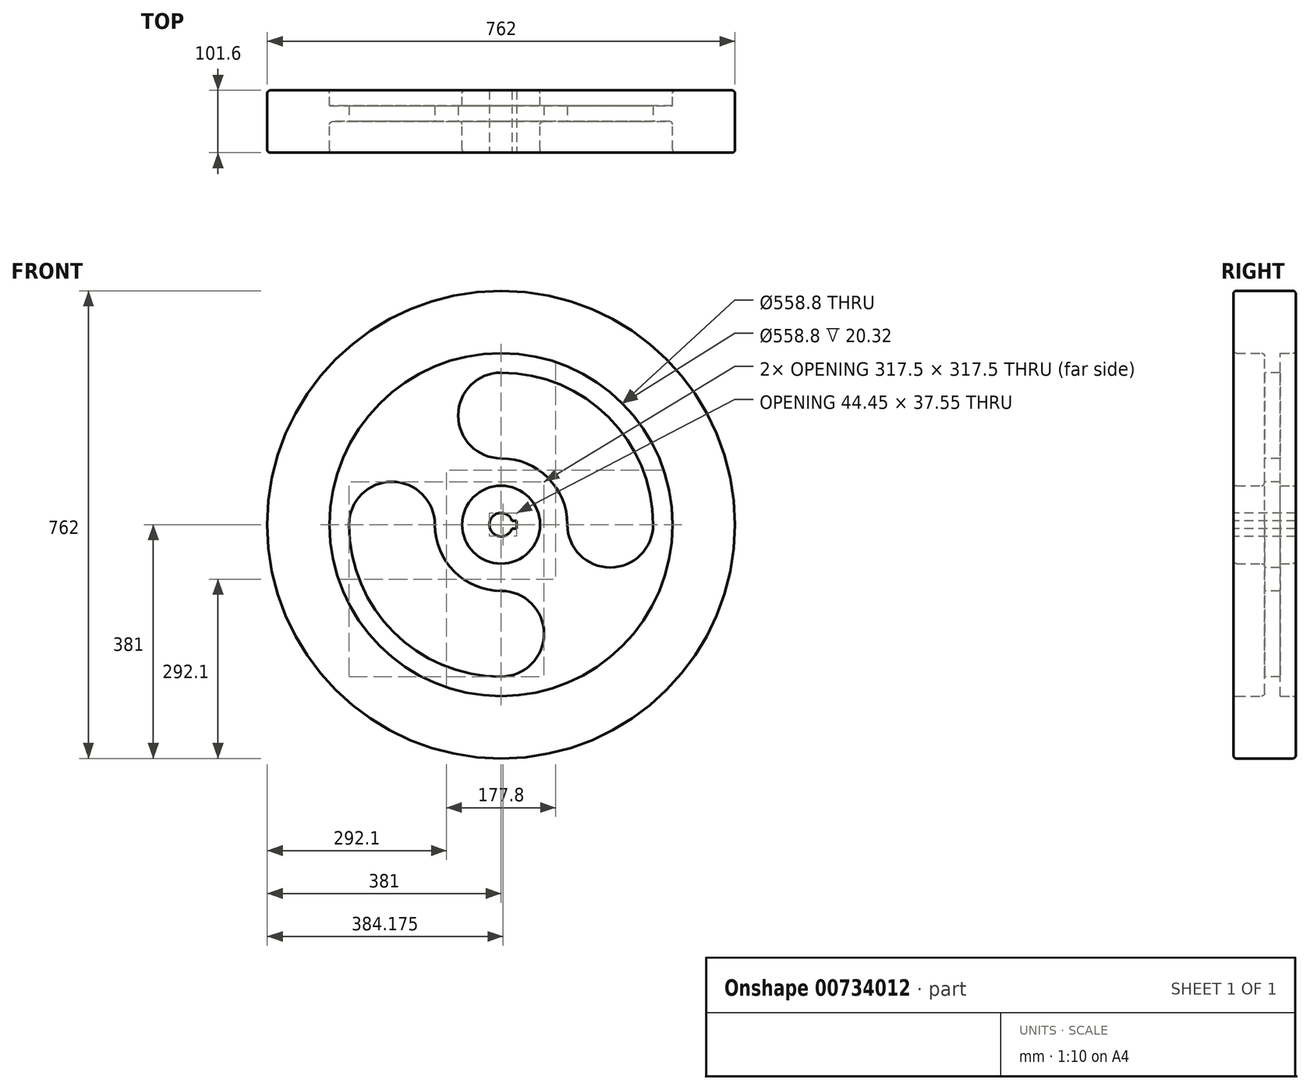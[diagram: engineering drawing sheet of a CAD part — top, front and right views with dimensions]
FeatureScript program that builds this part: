
annotation { "Feature Type Name" : "Feature", "Feature Type Description" : "" }
export const myFeature = defineFeature(function(context is Context, id is Id, definition is map)
    precondition{}
    {
        {
            var Q0;
            Q0=qCreatedBy(makeId("Front.planeOp"),FACE);
            var sketch = newSketch(context, id + "F0", { "sketchPlane" : qUnion([Q0])});
            skCircle(sketch, "E0", {"center": v(0, 0) * mm, "radius": 381 * mm});
            skSolve(sketch);
        }
        {
            var Q0;
            Q0 = qSketchRegion(id + "F0", true);
            extrude(context, id + "F1", {"entities" : qUnion([Q0]), "depth" : 25.4 * mm, "offsetDistance" : 25.4 * mm, "symmetric" : true});
        }
        {
            var Q0;
            Q0=makeQuery(id+"F1.opExtrude","CAP_FACE",FACE,{"disambiguationData":[OSD([sQuery(id+"F0.wireOp",EDGE,"E0")])],"isStart":false});
            var sketch = newSketch(context, id + "F2", { "sketchPlane" : qUnion([Q0])});
            skCircle(sketch, "E1", {"center": v(0, 0) * mm, "radius": 279.4 * mm});
            skCircle(sketch, "E2", {"center": v(0, 0) * mm, "radius": 63.5 * mm});
            skSolve(sketch);
        }
        {
            var Q0;
            Q0=makeQuery(id+"F2.imprint","IMPRINT",FACE,{"disambiguationData":[TD([[makeQuery(id+"F2.imprint","IMPRINT",EDGE,{"derivedFrom":sQuery(id+"F2.wireOp",EDGE,"E1")}),-1.0]])]});
            var Q1;
            Q1=makeQuery(id+"F2.imprint","IMPRINT",FACE,{"disambiguationData":[TD([[makeQuery(id+"F2.imprint","IMPRINT",EDGE,{"derivedFrom":sQuery(id+"F2.wireOp",EDGE,"E2")}),1.0]])]});
            extrude(context, id + "F3", {"entities" : qUnion([Q0, Q1]), "operationType" : NewBodyOperationType.ADD, "depth" : 101.6 * mm, "offsetDistance" : 25.4 * mm, "symmetric" : true});
        }
        {
            var Q0;
            Q0=makeQuery(id+"F1.opExtrude","CAP_FACE",FACE,{"disambiguationData":[OSD([sQuery(id+"F0.wireOp",EDGE,"E0")])],"isStart":false});
            var sketch = newSketch(context, id + "F4", { "sketchPlane" : qUnion([Q0])});
            skSolve(sketch);
        }
        {
            var Q0;
            Q0=makeQuery(id+"F4.imprint","IMPRINT",FACE,{"disambiguationData":[TD([[makeQuery(id+"F4.imprint","IMPRINT",EDGE,{"derivedFrom":makeQuery(id+"F3.boolean.opBoolean","INTERSECT",EDGE,{"derivedFrom":[makeQuery(id+"F1.opExtrude","CAP_FACE",FACE,{"disambiguationData":[OSD([sQuery(id+"F0.wireOp",EDGE,"E0")])],"isStart":false}),makeQuery(id+"F3.opExtrude","SWEPT_FACE",FACE,{"disambiguationData":[OSD([sQuery(id+"F2.wireOp",EDGE,"E1")])]})]})}),-1.0]])]});
            var sketch = newSketch(context, id + "F5", { "sketchPlane" : qUnion([Q0])});
            skCircle(sketch, "E3", {"center": v(0, 0) * mm, "radius": 177.8 * mm, "construction": true});
            skCircle(sketch, "E4", {"center": v(177.8, 0) * mm, "radius": 69.85 * mm});
            skCircle(sketch, "E5.1.0", {"center": v(0, 177.8) * mm, "radius": 69.85 * mm});
            skCircle(sketch, "E5.2.0", {"center": v(-177.8, 0) * mm, "radius": 69.85 * mm});
            skCircle(sketch, "E5.3.0", {"center": v(0, -177.8) * mm, "radius": 69.85 * mm});
            skCircle(sketch, "E6", {"center": v(0, 0) * mm, "radius": 247.65 * mm});
            skCircle(sketch, "E7", {"center": v(0, 0) * mm, "radius": 107.95 * mm});
            skSolve(sketch);
        }
        {
            var Q0;
            {var subQ0=sQuery(id+"F5.wireOp",EDGE,"E6");var subQ1=sQuery(id+"F5.wireOp",EDGE,"E4");var subQ2=makeQuery(id+"F5.imprint","INTERSECT",VERTEX,{"derivedFrom":[subQ1,subQ0]});Q0=makeQuery(id+"F5.imprint","IMPRINT",FACE,{"disambiguationData":[TD([[makeQuery(id+"F5.imprint","IMPRINT",EDGE,{"disambiguationData":[TD([[subQ2,-1.0]])],"derivedFrom":subQ1}),-1.0]])]});}
            var Q1;
            {var subQ0=sQuery(id+"F5.wireOp",EDGE,"E6");var subQ1=sQuery(id+"F5.wireOp",EDGE,"E5.2.0");var subQ2=makeQuery(id+"F5.imprint","INTERSECT",VERTEX,{"derivedFrom":[subQ1,subQ0]});Q1=makeQuery(id+"F5.imprint","IMPRINT",FACE,{"disambiguationData":[TD([[makeQuery(id+"F5.imprint","IMPRINT",EDGE,{"disambiguationData":[TD([[subQ2,-1.0]])],"derivedFrom":subQ1}),-1.0]])]});}
            var Q2;
            {var subQ0=sQuery(id+"F5.wireOp",EDGE,"E5.1.0");var subQ1=makeQuery(id+"F5.imprint","INTERSECT",VERTEX,{"derivedFrom":[subQ0,sQuery(id+"F5.wireOp",EDGE,"E6")]});Q2=makeQuery(id+"F5.imprint","IMPRINT",FACE,{"disambiguationData":[TD([[makeQuery(id+"F5.imprint","IMPRINT",EDGE,{"disambiguationData":[TD([[subQ1,-1.0]])],"derivedFrom":subQ0}),1.0]])]});}
            var Q3;
            {var subQ0=sQuery(id+"F5.wireOp",EDGE,"E5.2.0");var subQ1=makeQuery(id+"F5.imprint","INTERSECT",VERTEX,{"derivedFrom":[subQ0,sQuery(id+"F5.wireOp",EDGE,"E6")]});Q3=makeQuery(id+"F5.imprint","IMPRINT",FACE,{"disambiguationData":[TD([[makeQuery(id+"F5.imprint","IMPRINT",EDGE,{"disambiguationData":[TD([[subQ1,-1.0]])],"derivedFrom":subQ0}),1.0]])]});}
            var Q4;
            {var subQ0=sQuery(id+"F5.wireOp",EDGE,"E5.3.0");var subQ1=makeQuery(id+"F5.imprint","INTERSECT",VERTEX,{"derivedFrom":[subQ0,sQuery(id+"F5.wireOp",EDGE,"E6")]});Q4=makeQuery(id+"F5.imprint","IMPRINT",FACE,{"disambiguationData":[TD([[makeQuery(id+"F5.imprint","IMPRINT",EDGE,{"disambiguationData":[TD([[subQ1,-1.0]])],"derivedFrom":subQ0}),1.0]])]});}
            var Q5;
            {var subQ0=sQuery(id+"F5.wireOp",EDGE,"E5.4.0");var subQ1=makeQuery(id+"F5.imprint","INTERSECT",VERTEX,{"derivedFrom":[subQ0,sQuery(id+"F5.wireOp",EDGE,"E6")]});Q5=makeQuery(id+"F5.imprint","IMPRINT",FACE,{"disambiguationData":[TD([[makeQuery(id+"F5.imprint","IMPRINT",EDGE,{"disambiguationData":[TD([[subQ1,-1.0]])],"derivedFrom":subQ0}),1.0]])]});}
            var Q6;
            {var subQ0=sQuery(id+"F5.wireOp",EDGE,"E4");var subQ1=makeQuery(id+"F5.imprint","INTERSECT",VERTEX,{"derivedFrom":[subQ0,sQuery(id+"F5.wireOp",EDGE,"E6")]});Q6=makeQuery(id+"F5.imprint","IMPRINT",FACE,{"disambiguationData":[TD([[makeQuery(id+"F5.imprint","IMPRINT",EDGE,{"disambiguationData":[TD([[subQ1,-1.0]])],"derivedFrom":subQ0}),1.0]])]});}
            var Q7;
            {var subQ0=sQuery(id+"F5.wireOp",EDGE,"E6");var subQ1=sQuery(id+"F5.wireOp",EDGE,"E5.4.0");var subQ2=makeQuery(id+"F5.imprint","INTERSECT",VERTEX,{"derivedFrom":[subQ1,subQ0]});Q7=makeQuery(id+"F5.imprint","IMPRINT",FACE,{"disambiguationData":[TD([[makeQuery(id+"F5.imprint","IMPRINT",EDGE,{"disambiguationData":[TD([[subQ2,-1.0]])],"derivedFrom":subQ1}),-1.0]])]});}
            var Q8;
            {var subQ0=sQuery(id+"F5.wireOp",EDGE,"E5.5.0");var subQ1=makeQuery(id+"F5.imprint","INTERSECT",VERTEX,{"derivedFrom":[subQ0,sQuery(id+"F5.wireOp",EDGE,"E6")]});Q8=makeQuery(id+"F5.imprint","IMPRINT",FACE,{"disambiguationData":[TD([[makeQuery(id+"F5.imprint","IMPRINT",EDGE,{"disambiguationData":[TD([[subQ1,-1.0]])],"derivedFrom":subQ0}),1.0]])]});}
            extrude(context, id + "F6", {"entities" : qUnion([Q0, Q1, Q2, Q3, Q4, Q5, Q6, Q7, Q8]), "operationType" : NewBodyOperationType.REMOVE, "oppositeDirection" : true, "depth" : 25.4 * mm, "offsetDistance" : 25.4 * mm});
        }
        {
            var Q0;
            Q0=makeQuery(id+"F3.boolean.opBoolean","INTERSECT",EDGE,{"derivedFrom":[makeQuery(id+"F1.opExtrude","CAP_FACE",FACE,{"disambiguationData":[OSD([sQuery(id+"F0.wireOp",EDGE,"E0")])],"isStart":false}),makeQuery(id+"F3.opExtrude","SWEPT_FACE",FACE,{"disambiguationData":[OSD([sQuery(id+"F2.wireOp",EDGE,"E2")])]})]});
            var Q1;
            Q1=makeQuery(id+"F3.opExtrude","CAP_EDGE",EDGE,{"disambiguationData":[OSD([sQuery(id+"F2.wireOp",EDGE,"E1")])],"isStart":false});
            var Q2;
            Q2=makeQuery(id+"F3.opExtrude","CAP_EDGE",EDGE,{"disambiguationData":[OSD([sQuery(id+"F0.wireOp",EDGE,"E0")])],"isStart":false});
            var Q3;
            Q3=makeQuery(id+"F3.opExtrude","CAP_EDGE",EDGE,{"disambiguationData":[OSD([sQuery(id+"F2.wireOp",EDGE,"E2")])],"isStart":true});
            var Q4;
            Q4=makeQuery(id+"F3.opExtrude","CAP_EDGE",EDGE,{"disambiguationData":[OSD([sQuery(id+"F0.wireOp",EDGE,"E0")])],"isStart":true});
            var Q5;
            Q5=makeQuery(id+"F3.opExtrude","CAP_EDGE",EDGE,{"disambiguationData":[OSD([sQuery(id+"F2.wireOp",EDGE,"E1")])],"isStart":true});
            var Q6;
            Q6=makeQuery(id+"F3.boolean.opBoolean","INTERSECT",EDGE,{"derivedFrom":[makeQuery(id+"F1.opExtrude","CAP_FACE",FACE,{"disambiguationData":[OSD([sQuery(id+"F0.wireOp",EDGE,"E0")])],"isStart":false}),makeQuery(id+"F3.opExtrude","SWEPT_FACE",FACE,{"disambiguationData":[OSD([sQuery(id+"F2.wireOp",EDGE,"E1")])]})]});
            var Q7;
            Q7=makeQuery(id+"F3.opExtrude","CAP_EDGE",EDGE,{"disambiguationData":[OSD([sQuery(id+"F2.wireOp",EDGE,"E2")])],"isStart":false});
            fillet(context, id + "F7", {"entities" : qUnion([Q0, Q1, Q2, Q3, Q4, Q5, Q6, Q7]), "radius" : 5.08 * mm, "tangentPropagation" : true, "allowEdgeOverflow" : false});
        }
        {
            var Q0;
            Q0=makeQuery(id+"F3.opExtrude","CAP_FACE",FACE,{"disambiguationData":[OSD([sQuery(id+"F2.wireOp",EDGE,"E2")])],"isStart":false});
            var sketch = newSketch(context, id + "F8", { "sketchPlane" : qUnion([Q0])});
            skCircle(sketch, "E8", {"center": v(0, 0) * mm, "radius": 19.05 * mm});
            skLineSegment(sketch, "E9.bottom", {"start": v(25.4, -6.35) * mm, "end": v(-6.56, -6.35) * mm});
            skLineSegment(sketch, "E9.top", {"start": v(25.4, 6.35) * mm, "end": v(-6.56, 6.35) * mm});
            skLineSegment(sketch, "E9.left", {"start": v(25.4, -6.35) * mm, "end": v(25.4, 6.35) * mm});
            skLineSegment(sketch, "E9.right", {"start": v(-6.56, -6.35) * mm, "end": v(-6.56, 6.35) * mm});
            skPoint(sketch, "E9.middle", {"position": v(9.42, 0) * mm});
            skSolve(sketch);
        }
        {
            var Q0;
            Q0 = qSketchRegion(id + "F8", true);
            extrude(context, id + "F9", {"entities" : qUnion([Q0]), "operationType" : NewBodyOperationType.REMOVE, "oppositeDirection" : true, "depth" : 101.6 * mm, "offsetDistance" : 25.4 * mm});
        }
    });
